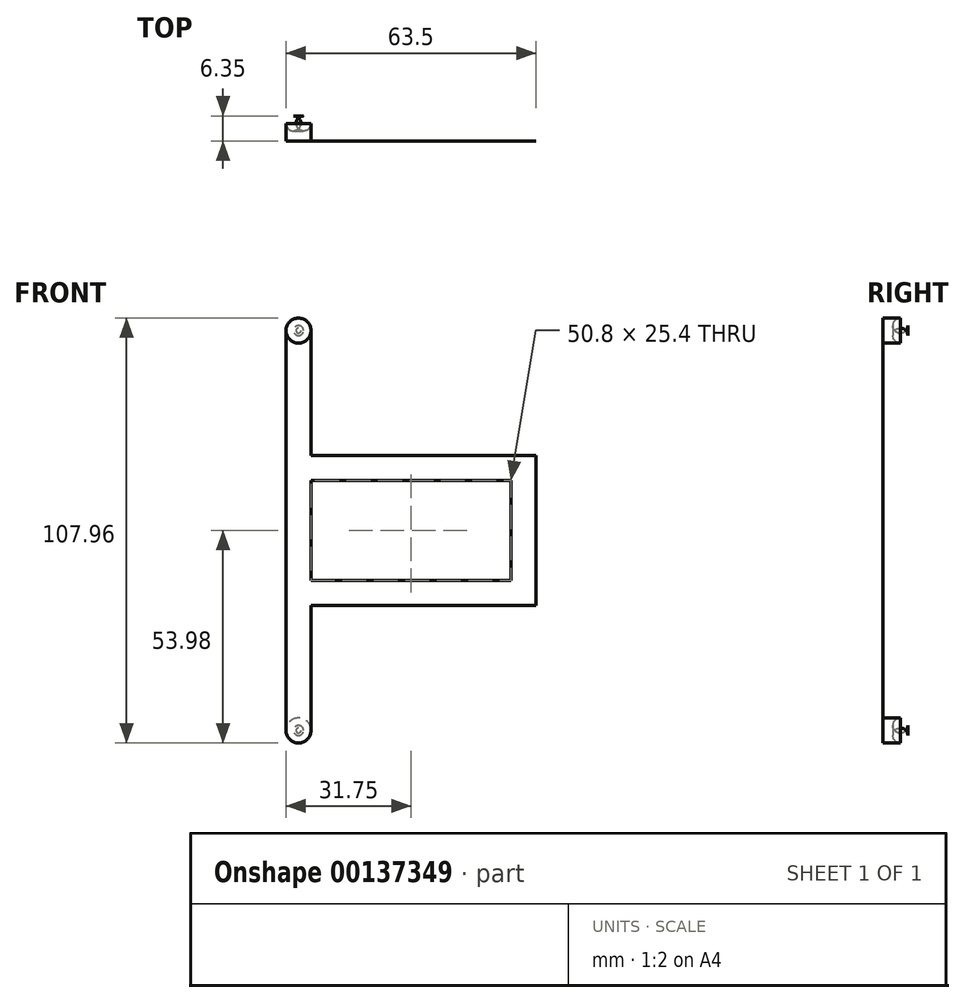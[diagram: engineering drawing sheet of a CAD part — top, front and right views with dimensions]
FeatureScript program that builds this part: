
annotation { "Feature Type Name" : "Feature", "Feature Type Description" : "" }
export const myFeature = defineFeature(function(context is Context, id is Id, definition is map)
    precondition{}
    {
        {
            var Q0;
            Q0=qCreatedBy(makeId("Front.planeOp"),FACE);
            var sketch = newSketch(context, id + "F3", { "sketchPlane" : qUnion([Q0])});
            skLineSegment(sketch, "E0", {"start": v(0, 50.8) * mm, "end": v(0, -50.8) * mm});
            skLineSegment(sketch, "E1", {"start": v(0, -50.8) * mm, "end": v(6.35, -50.8) * mm});
            skLineSegment(sketch, "E2", {"start": v(6.35, -50.8) * mm, "end": v(6.35, -19.05) * mm});
            skLineSegment(sketch, "E3", {"start": v(6.35, -19.05) * mm, "end": v(63.5, -19.05) * mm});
            skLineSegment(sketch, "E4", {"start": v(63.5, -19.05) * mm, "end": v(63.5, 19.05) * mm});
            skLineSegment(sketch, "E5", {"start": v(63.5, 19.05) * mm, "end": v(6.35, 19.05) * mm});
            skLineSegment(sketch, "E6", {"start": v(6.35, 19.05) * mm, "end": v(6.35, 50.8) * mm});
            skLineSegment(sketch, "E7", {"start": v(6.35, 50.8) * mm, "end": v(0, 50.8) * mm});
            skLineSegment(sketch, "E8", {"start": v(-52.05, 0) * mm, "end": v(33.37, 0) * mm});
            skLineSegment(sketch, "E9.bottom", {"start": v(6.35, 12.7) * mm, "end": v(57.15, 12.7) * mm});
            skLineSegment(sketch, "E9.top", {"start": v(6.35, -12.7) * mm, "end": v(57.15, -12.7) * mm});
            skLineSegment(sketch, "E9.left", {"start": v(6.35, 12.7) * mm, "end": v(6.35, -12.7) * mm});
            skLineSegment(sketch, "E9.right", {"start": v(57.15, 12.7) * mm, "end": v(57.15, -12.7) * mm});
            skSolve(sketch);
        }
        {
            var Q0;
            Q0 = qSketchRegion(id + "F3", true);
            extrude(context, id + "F0", {"entities" : qUnion([Q0]), "depth" : 1 / 203.2 * mm});
        }
        {
            var Q0;
            Q0=makeQuery(id+"F0.opExtrude","CAP_FACE",FACE,{"disambiguationData":[OSD([sQuery(id+"F3.wireOp",EDGE,"E0"),sQuery(id+"F3.wireOp",EDGE,"E1"),sQuery(id+"F3.wireOp",EDGE,"E2"),sQuery(id+"F3.wireOp",EDGE,"E3"),sQuery(id+"F3.wireOp",EDGE,"E4"),sQuery(id+"F3.wireOp",EDGE,"E5"),sQuery(id+"F3.wireOp",EDGE,"E6"),sQuery(id+"F3.wireOp",EDGE,"E7"),sQuery(id+"F3.wireOp",EDGE,"E9.bottom"),sQuery(id+"F3.wireOp",EDGE,"E9.top"),sQuery(id+"F3.wireOp",EDGE,"E9.left"),sQuery(id+"F3.wireOp",EDGE,"E9.right")])],"isStart":false});
            var sketch = newSketch(context, id + "F1", { "sketchPlane" : qUnion([Q0])});
            skCircle(sketch, "E10", {"center": v(3.18, -50.8) * mm, "radius": 3.17 * mm});
            skCircle(sketch, "E11", {"center": v(3.18, 50.8) * mm, "radius": 3.17 * mm});
            skSolve(sketch);
        }
        {
            var Q0;
            Q0 = qSketchRegion(id + "F1", true);
            extrude(context, id + "F4", {"entities" : qUnion([Q0]), "operationType" : NewBodyOperationType.ADD, "oppositeDirection" : true, "depth" : 6.35 * mm});
        }
        {
            var Q0;
            Q0=makeQuery(id+"F4.opExtrude","CAP_EDGE",EDGE,{"disambiguationData":[OSD([sQuery(id+"F1.wireOp",EDGE,"E11")])],"isStart":false});
            var Q1;
            Q1=makeQuery(id+"F4.opExtrude","CAP_EDGE",EDGE,{"disambiguationData":[OSD([sQuery(id+"F1.wireOp",EDGE,"E10")])],"isStart":false});
            fillet(context, id + "F2", {"entities" : qUnion([Q0, Q1]), "radius" : 1.9 * mm, "tangentPropagation" : true, "allowEdgeOverflow" : false});
        }
    });
